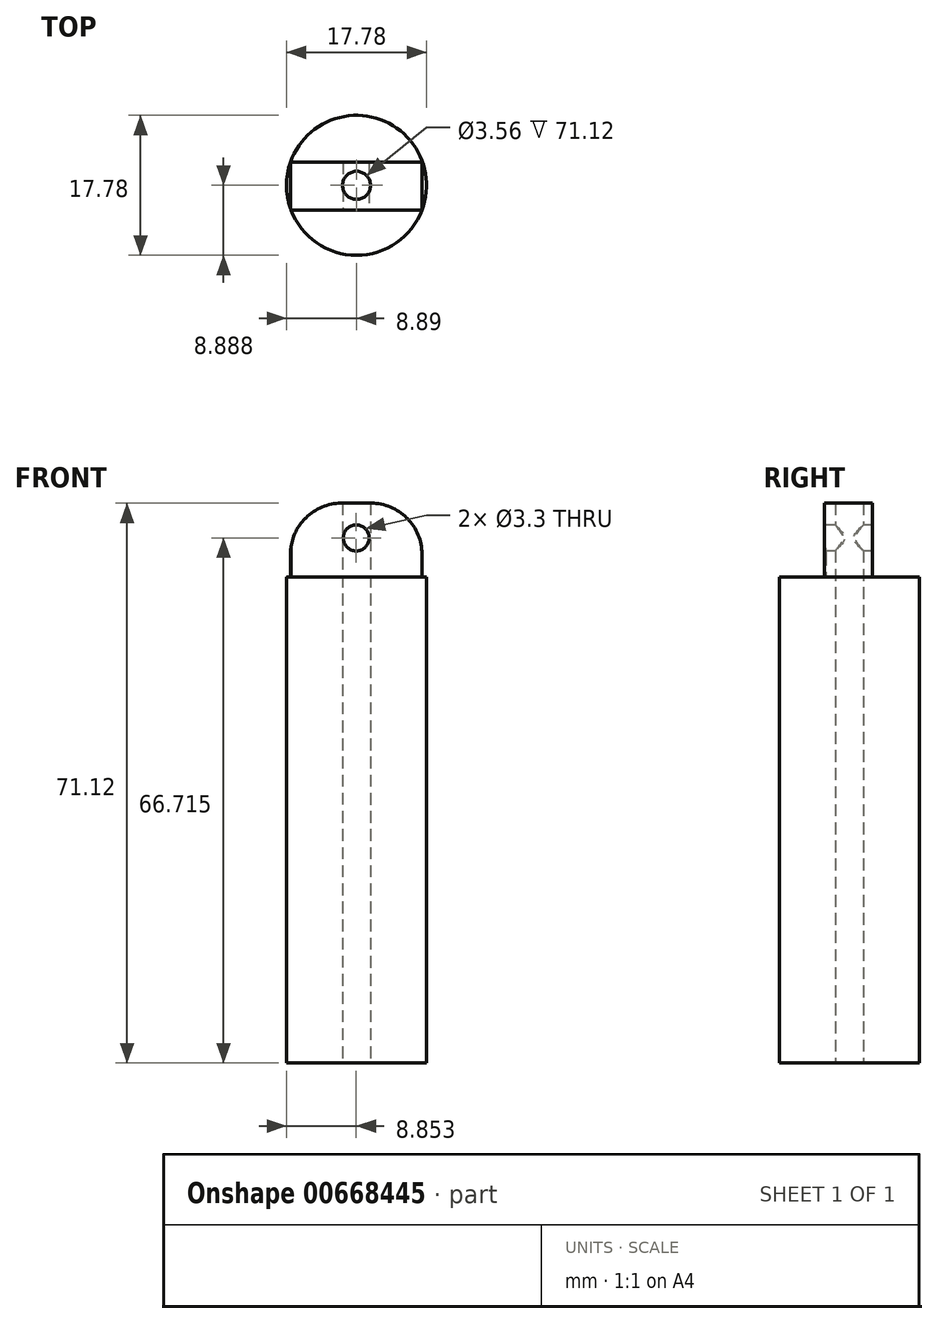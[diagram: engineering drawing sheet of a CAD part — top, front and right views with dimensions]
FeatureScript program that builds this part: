
annotation { "Feature Type Name" : "Feature", "Feature Type Description" : "" }
export const myFeature = defineFeature(function(context is Context, id is Id, definition is map)
    precondition{}
    {
        {
            var Q0;
            Q0=qCreatedBy(makeId("Top.planeOp"),FACE);
            var sketch = newSketch(context, id + "F0", { "sketchPlane" : qUnion([Q0])});
            skCircle(sketch, "E0", {"center": v(-23.34, 17.46) * mm, "radius": 8.89 * mm});
            skCircle(sketch, "E1", {"center": v(-23.34, 17.46) * mm, "radius": 1.78 * mm});
            skSolve(sketch);
        }
        {
            var Q0;
            Q0=makeQuery(id+"F0.imprint","IMPRINT",FACE,{"disambiguationData":[TD([[makeQuery(id+"F0.imprint","IMPRINT",EDGE,{"derivedFrom":sQuery(id+"F0.wireOp",EDGE,"E0")}),1.0]])]});
            extrude(context, id + "F1", {"entities" : qUnion([Q0]), "depth" : 61.72 * mm});
        }
        {
            var Q0;
            Q0=makeQuery(id+"F1.opExtrude","CAP_FACE",FACE,{"disambiguationData":[OSD([sQuery(id+"F0.wireOp",EDGE,"E0"),sQuery(id+"F0.wireOp",EDGE,"E1")])],"isStart":false});
            var sketch = newSketch(context, id + "F2", { "sketchPlane" : qUnion([Q0])});
            skLineSegment(sketch, "E2.bottom", {"start": v(-31.73, 20.4) * mm, "end": v(-15.02, 20.4) * mm});
            skLineSegment(sketch, "E2.top", {"start": v(-31.73, 14.32) * mm, "end": v(-15.02, 14.32) * mm});
            skLineSegment(sketch, "E2.left", {"start": v(-31.73, 20.4) * mm, "end": v(-31.73, 14.32) * mm});
            skLineSegment(sketch, "E2.right", {"start": v(-15.02, 20.4) * mm, "end": v(-15.02, 14.32) * mm});
            skSolve(sketch);
        }
        {
            var Q0;
            {var subQ1=sQuery(id+"F2.wireOp",EDGE,"E2.bottom");Q0=makeQuery(id+"F2.imprint","IMPRINT",FACE,{"disambiguationData":[TD([[makeQuery(id+"F2.imprint","IMPRINT",EDGE,{"derivedFrom":subQ1}),-1.0]])]});}
            extrude(context, id + "F3", {"entities" : qUnion([Q0]), "operationType" : NewBodyOperationType.ADD, "depth" : 9.4 * mm});
        }
        {
            var Q0;
            Q0=makeQuery(id+"F3.opExtrude","CAP_EDGE",EDGE,{"disambiguationData":[OSD([sQuery(id+"F2.wireOp",EDGE,"E2.right")])],"isStart":false});
            var Q1;
            Q1=makeQuery(id+"F3.opExtrude","CAP_EDGE",EDGE,{"disambiguationData":[OSD([sQuery(id+"F2.wireOp",EDGE,"E2.left")])],"isStart":false});
            chamfer(context, id + "F4", {"entities" : qUnion([Q0, Q1]), "width" : 3.8 * mm, "tangentPropagation" : true});
        }
        {
            var Q0;
            {var subQ0=sQuery(id+"F2.wireOp",EDGE,"E2.left");Q0=makeQuery(id+"F4.opChamfer","BLEND_EDGE",EDGE,{"blendedFrom":[makeQuery(id+"F3.opExtrude","CAP_EDGE",EDGE,{"disambiguationData":[OSD([subQ0])],"isStart":false}),makeQuery(id+"F3.opExtrude","CAP_FACE",FACE,{"disambiguationData":[OSD([sQuery(id+"F0.wireOp",EDGE,"E0"),sQuery(id+"F0.wireOp",EDGE,"E1"),sQuery(id+"F2.wireOp",EDGE,"E2.bottom"),sQuery(id+"F2.wireOp",EDGE,"E2.top"),subQ0,sQuery(id+"F2.wireOp",EDGE,"E2.right")])],"isStart":false})],"blendedInto":[makeQuery(id+"F3.opExtrude","CAP_FACE",FACE,{"disambiguationData":[OSD([sQuery(id+"F0.wireOp",EDGE,"E0"),sQuery(id+"F0.wireOp",EDGE,"E1"),sQuery(id+"F2.wireOp",EDGE,"E2.bottom"),sQuery(id+"F2.wireOp",EDGE,"E2.top"),subQ0,sQuery(id+"F2.wireOp",EDGE,"E2.right")])],"isStart":false})]});}
            var Q1;
            {var subQ0=sQuery(id+"F2.wireOp",EDGE,"E2.right");Q1=makeQuery(id+"F4.opChamfer","BLEND_EDGE",EDGE,{"blendedFrom":[makeQuery(id+"F3.opExtrude","CAP_EDGE",EDGE,{"disambiguationData":[OSD([subQ0])],"isStart":false}),makeQuery(id+"F3.opExtrude","CAP_FACE",FACE,{"disambiguationData":[OSD([sQuery(id+"F0.wireOp",EDGE,"E0"),sQuery(id+"F0.wireOp",EDGE,"E1"),sQuery(id+"F2.wireOp",EDGE,"E2.bottom"),sQuery(id+"F2.wireOp",EDGE,"E2.top"),sQuery(id+"F2.wireOp",EDGE,"E2.left"),subQ0])],"isStart":false})],"blendedInto":[makeQuery(id+"F3.opExtrude","CAP_FACE",FACE,{"disambiguationData":[OSD([sQuery(id+"F0.wireOp",EDGE,"E0"),sQuery(id+"F0.wireOp",EDGE,"E1"),sQuery(id+"F2.wireOp",EDGE,"E2.bottom"),sQuery(id+"F2.wireOp",EDGE,"E2.top"),sQuery(id+"F2.wireOp",EDGE,"E2.left"),subQ0])],"isStart":false})]});}
            var Q2;
            {var subQ0=sQuery(id+"F2.wireOp",EDGE,"E2.right");Q2=makeQuery(id+"F4.opChamfer","BLEND_EDGE",EDGE,{"blendedFrom":[makeQuery(id+"F3.opExtrude","CAP_EDGE",EDGE,{"disambiguationData":[OSD([subQ0])],"isStart":false}),makeQuery(id+"F3.opExtrude","SWEPT_FACE",FACE,{"disambiguationData":[OSD([subQ0])]})],"blendedInto":[makeQuery(id+"F3.opExtrude","SWEPT_FACE",FACE,{"disambiguationData":[OSD([subQ0])]})]});}
            var Q3;
            {var subQ0=sQuery(id+"F2.wireOp",EDGE,"E2.left");Q3=makeQuery(id+"F4.opChamfer","BLEND_EDGE",EDGE,{"blendedFrom":[makeQuery(id+"F3.opExtrude","CAP_EDGE",EDGE,{"disambiguationData":[OSD([subQ0])],"isStart":false}),makeQuery(id+"F3.opExtrude","SWEPT_FACE",FACE,{"disambiguationData":[OSD([subQ0])]})],"blendedInto":[makeQuery(id+"F3.opExtrude","SWEPT_FACE",FACE,{"disambiguationData":[OSD([subQ0])]})]});}
            fillet(context, id + "F5", {"entities" : qUnion([Q0, Q1, Q2, Q3]), "radius" : 6.35 * mm, "tangentPropagation" : true, "allowEdgeOverflow" : false});
        }
        {
            var Q0;
            Q0=makeQuery(id+"F3.opExtrude","SWEPT_FACE",FACE,{"disambiguationData":[OSD([sQuery(id+"F2.wireOp",EDGE,"E2.top")])]});
            var sketch = newSketch(context, id + "F6", { "sketchPlane" : qUnion([Q0])});
            skCircle(sketch, "E3", {"center": v(-23.38, 66.71) * mm, "radius": 3.18 * mm});
            skPoint(sketch, "E3.centerSnap0", {"position": v(-23.38, 71.12) * mm});
            skSolve(sketch);
        }
        {
            var Q0;
            Q0=sQuery(id+"F6.wireOp",VERTEX,"E3.center");
            var Q1;
            Q1=makeQuery(id+"F1.opExtrude","SWEPT_BODY",BODY,{"disambiguationData":[OSD([sQuery(id+"F0.wireOp",EDGE,"E0"),sQuery(id+"F0.wireOp",EDGE,"E1")])]});
            hole(context, id + "F7", {"style" : HoleStyle.SIMPLE, "endStyle" : HoleEndStyle.THROUGH, "standardTappedOrClearance" : lookupTablePath({ "standard" : "ISO", "fit" : "Normal", "size" : "M3", "type" : "Clearance" }), "standardBlindInLast" : lookupTablePath({ "fit" : "Standard", "standard" : "ISO", "size" : "M3", "type" : "Clearance" }), "holeDiameter" : 3.3 * mm, "isTappedThrough" : true, "tappedDepth" : 12.7 * mm, "tapClearance" : 3, "locations" : qUnion([Q0]), "scope" : qUnion([Q1])});
        }
    });
